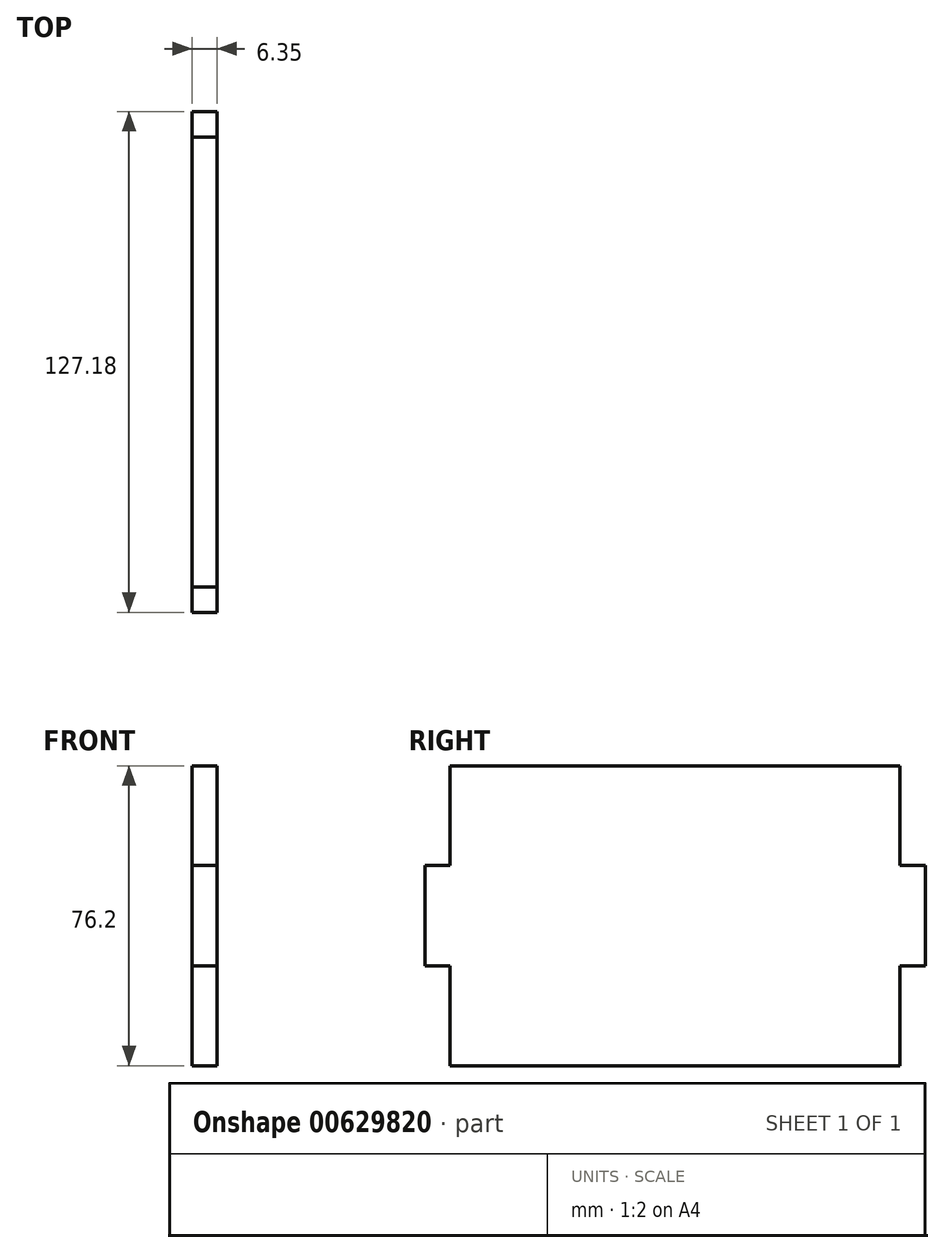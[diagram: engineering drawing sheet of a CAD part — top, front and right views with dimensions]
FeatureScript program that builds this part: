
annotation { "Feature Type Name" : "Feature", "Feature Type Description" : "" }
export const myFeature = defineFeature(function(context is Context, id is Id, definition is map)
    precondition{}
    {
        {
            var Q0;
            Q0=qCreatedBy(makeId("Right.planeOp"),FACE);
            var sketch = newSketch(context, id + "F0", { "sketchPlane" : qUnion([Q0])});
            skLineSegment(sketch, "E0.bottom", {"start": v(0, 0) * mm, "end": v(114.3, 0) * mm});
            skLineSegment(sketch, "E0.top", {"start": v(0, 76.2) * mm, "end": v(114.3, 76.2) * mm});
            skLineSegment(sketch, "E0.left", {"start": v(0, 0) * mm, "end": v(0, 76.2) * mm});
            skLineSegment(sketch, "E0.right", {"start": v(114.3, 0) * mm, "end": v(114.3, 76.2) * mm});
            skLineSegment(sketch, "E1.bottom", {"start": v(0, 50.89) * mm, "end": v(-6.44, 50.89) * mm});
            skLineSegment(sketch, "E1.top", {"start": v(0, 25.31) * mm, "end": v(-6.44, 25.31) * mm});
            skLineSegment(sketch, "E1.left", {"start": v(0, 50.89) * mm, "end": v(0, 25.31) * mm});
            skLineSegment(sketch, "E1.right", {"start": v(-6.44, 50.89) * mm, "end": v(-6.44, 25.31) * mm});
            skLineSegment(sketch, "E2.bottom", {"start": v(114.3, 50.89) * mm, "end": v(120.74, 50.89) * mm});
            skLineSegment(sketch, "E2.top", {"start": v(114.3, 25.31) * mm, "end": v(120.74, 25.31) * mm});
            skLineSegment(sketch, "E2.left", {"start": v(114.3, 50.89) * mm, "end": v(114.3, 25.31) * mm});
            skLineSegment(sketch, "E2.right", {"start": v(120.74, 50.89) * mm, "end": v(120.74, 25.31) * mm});
            skLineSegment(sketch, "E3.bottom", {"start": v(18.96, 0) * mm, "end": v(44.54, 0) * mm});
            skLineSegment(sketch, "E3.top", {"start": v(18.96, -6.44) * mm, "end": v(44.54, -6.44) * mm});
            skLineSegment(sketch, "E3.left", {"start": v(18.96, 0) * mm, "end": v(18.96, -6.44) * mm});
            skLineSegment(sketch, "E3.right", {"start": v(44.54, 0) * mm, "end": v(44.54, -6.44) * mm});
            skLineSegment(sketch, "E4.bottom", {"start": v(69.76, 0) * mm, "end": v(95.34, 0) * mm});
            skLineSegment(sketch, "E4.top", {"start": v(69.76, -6.44) * mm, "end": v(95.34, -6.44) * mm});
            skLineSegment(sketch, "E4.left", {"start": v(69.76, 0) * mm, "end": v(69.76, -6.44) * mm});
            skLineSegment(sketch, "E4.right", {"start": v(95.34, 0) * mm, "end": v(95.34, -6.44) * mm});
            skPoint(sketch, "E5", {"position": v(120.74, 38.1) * mm});
            skPoint(sketch, "E6", {"position": v(-6.44, 38.1) * mm});
            skPoint(sketch, "E7", {"position": v(31.75, -6.44) * mm});
            skPoint(sketch, "E8", {"position": v(82.55, -6.44) * mm});
            skSolve(sketch);
        }
        {
            var Q0;
            {var subQ2=sQuery(id+"F0.wireOp",EDGE,"E0.top");Q0=makeQuery(id+"F0.imprint","IMPRINT",FACE,{"disambiguationData":[TD([[makeQuery(id+"F0.imprint","IMPRINT",EDGE,{"derivedFrom":subQ2}),-1.0]])]});}
            var Q1;
            Q1=makeQuery(id+"F0.imprint","IMPRINT",FACE,{"disambiguationData":[TD([[makeQuery(id+"F0.imprint","IMPRINT",EDGE,{"derivedFrom":sQuery(id+"F0.wireOp",EDGE,"E1.bottom")}),1.0]])]});
            var Q2;
            Q2=makeQuery(id+"F0.imprint","IMPRINT",FACE,{"disambiguationData":[TD([[makeQuery(id+"F0.imprint","IMPRINT",EDGE,{"derivedFrom":sQuery(id+"F0.wireOp",EDGE,"E3.bottom")}),-1.0]])]});
            var Q3;
            Q3=makeQuery(id+"F0.imprint","IMPRINT",FACE,{"disambiguationData":[TD([[makeQuery(id+"F0.imprint","IMPRINT",EDGE,{"derivedFrom":sQuery(id+"F0.wireOp",EDGE,"E4.bottom")}),-1.0]])]});
            var Q4;
            Q4=makeQuery(id+"F0.imprint","IMPRINT",FACE,{"disambiguationData":[TD([[makeQuery(id+"F0.imprint","IMPRINT",EDGE,{"derivedFrom":sQuery(id+"F0.wireOp",EDGE,"E2.bottom")}),-1.0]])]});
            extrude(context, id + "F1", {"entities" : qUnion([Q0, Q1, Q2, Q3, Q4]), "depth" : 6.35 * mm, "offsetDistance" : 25.4 * mm});
        }
    });
